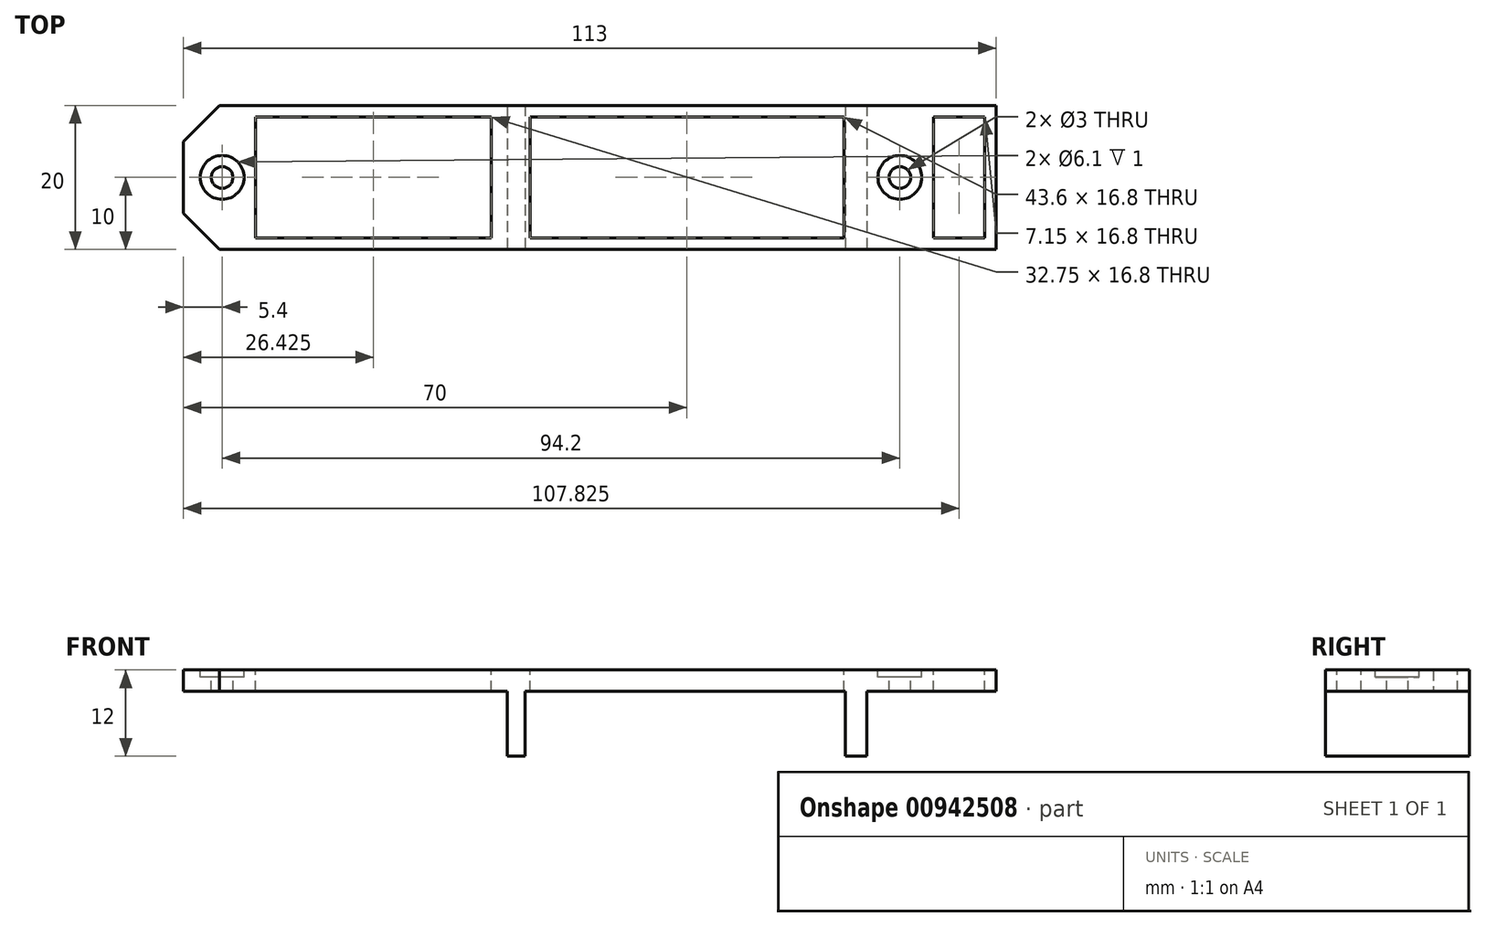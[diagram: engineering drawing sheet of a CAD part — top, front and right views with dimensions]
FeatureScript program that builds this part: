
annotation { "Feature Type Name" : "Feature", "Feature Type Description" : "" }
export const myFeature = defineFeature(function(context is Context, id is Id, definition is map)
    precondition{}
    {
        {
            var Q0;
            Q0=qCreatedBy(makeId("Top.planeOp"),FACE);
            var sketch = newSketch(context, id + "F0", { "sketchPlane" : qUnion([Q0])});
            skLineSegment(sketch, "E0.bottom", {"start": v(56.5, -10) * mm, "end": v(-56.5, -10) * mm});
            skLineSegment(sketch, "E0.top", {"start": v(56.5, 10) * mm, "end": v(-56.5, 10) * mm});
            skLineSegment(sketch, "E0.left", {"start": v(56.5, -10) * mm, "end": v(56.5, 10) * mm});
            skLineSegment(sketch, "E0.right", {"start": v(-56.5, -10) * mm, "end": v(-56.5, 10) * mm});
            skPoint(sketch, "E0.middle", {"position": v(0, 0) * mm});
            skSolve(sketch);
        }
        {
            var Q0;
            Q0=makeQuery(id+"F0.imprint","IMPRINT",FACE,{"disambiguationData":[TD([[makeQuery(id+"F0.imprint","IMPRINT",EDGE,{"derivedFrom":sQuery(id+"F0.wireOp",EDGE,"E0.bottom")}),-1.0]])]});
            extrude(context, id + "F1", {"entities" : qUnion([Q0]), "depth" : 3 * mm, "offsetDistance" : 25 * mm});
        }
        {
            var Q0;
            Q0=makeQuery(id+"F1.opExtrude","CAP_FACE",FACE,{"disambiguationData":[OSD([sQuery(id+"F0.wireOp",EDGE,"E0.bottom"),sQuery(id+"F0.wireOp",EDGE,"E0.top"),sQuery(id+"F0.wireOp",EDGE,"E0.left"),sQuery(id+"F0.wireOp",EDGE,"E0.right")])],"isStart":false});
            var sketch = newSketch(context, id + "F2", { "sketchPlane" : qUnion([Q0])});
            skLineSegment(sketch, "E1.bottom", {"start": v(35.5, 10) * mm, "end": v(38.5, 10) * mm});
            skLineSegment(sketch, "E1.top", {"start": v(35.5, -10) * mm, "end": v(38.5, -10) * mm});
            skLineSegment(sketch, "E1.left", {"start": v(35.5, 10) * mm, "end": v(35.5, -10) * mm});
            skLineSegment(sketch, "E1.right", {"start": v(38.5, 10) * mm, "end": v(38.5, -10) * mm});
            skPoint(sketch, "E1.middle", {"position": v(37, 0) * mm});
            skLineSegment(sketch, "E2.bottom", {"start": v(-9, 10) * mm, "end": v(-11.5, 10) * mm});
            skLineSegment(sketch, "E2.top", {"start": v(-9, -10) * mm, "end": v(-11.5, -10) * mm});
            skLineSegment(sketch, "E2.left", {"start": v(-9, 10) * mm, "end": v(-9, -10) * mm});
            skLineSegment(sketch, "E2.right", {"start": v(-11.5, 10) * mm, "end": v(-11.5, -10) * mm});
            skPoint(sketch, "E2.middle", {"position": v(-10.25, 0) * mm});
            skSolve(sketch);
        }
        {
            var Q0;
            Q0=makeQuery(id+"F2.imprint","IMPRINT",FACE,{"disambiguationData":[TD([[makeQuery(id+"F2.imprint","IMPRINT",EDGE,{"derivedFrom":sQuery(id+"F2.wireOp",EDGE,"E2.bottom")}),1.0]])]});
            var Q1;
            Q1=makeQuery(id+"F2.imprint","IMPRINT",FACE,{"disambiguationData":[TD([[makeQuery(id+"F2.imprint","IMPRINT",EDGE,{"derivedFrom":sQuery(id+"F2.wireOp",EDGE,"E1.bottom")}),1.0]])]});
            extrude(context, id + "F3", {"entities" : qUnion([Q0, Q1]), "operationType" : NewBodyOperationType.ADD, "oppositeDirection" : true, "depth" : 12 * mm, "offsetDistance" : 25 * mm});
        }
        {
            var Q0;
            {var subQ0=sQuery(id+"F0.wireOp",EDGE,"E0.top");var subQ1=sQuery(id+"F0.wireOp",EDGE,"E0.right");var subQ2=sQuery(id+"F0.wireOp",EDGE,"E0.bottom");Q0=makeQuery(id+"F3.boolean.opBoolean","SPLIT",FACE,{"disambiguationData":[TD([makeQuery(id+"F1.opExtrude","SWEPT_FACE",FACE,{"disambiguationData":[OSD([subQ1])]})])],"derivedFrom":makeQuery(id+"F1.opExtrude","CAP_FACE",FACE,{"disambiguationData":[OSD([subQ2,subQ0,sQuery(id+"F0.wireOp",EDGE,"E0.left"),subQ1])],"isStart":false})});}
            var sketch = newSketch(context, id + "F4", { "sketchPlane" : qUnion([Q0])});
            skCircle(sketch, "E3", {"center": v(-51.1, 0) * mm, "radius": 1.5 * mm});
            skCircle(sketch, "E4", {"center": v(43.1, 0) * mm, "radius": 1.5 * mm});
            skSolve(sketch);
        }
        {
            var Q0;
            Q0=makeQuery(id+"F4.imprint","IMPRINT",FACE,{"disambiguationData":[TD([[makeQuery(id+"F4.imprint","IMPRINT",EDGE,{"derivedFrom":sQuery(id+"F4.wireOp",EDGE,"E3")}),1.0]])]});
            var Q1;
            Q1=makeQuery(id+"F4.imprint","IMPRINT",FACE,{"disambiguationData":[TD([[makeQuery(id+"F4.imprint","IMPRINT",EDGE,{"derivedFrom":sQuery(id+"F4.wireOp",EDGE,"E4")}),1.0]])]});
            extrude(context, id + "F5", {"entities" : qUnion([Q0, Q1]), "operationType" : NewBodyOperationType.REMOVE, "endBound" : BoundingType.UP_TO_NEXT, "oppositeDirection" : true, "depth" : 25 * mm, "offsetDistance" : 25 * mm});
        }
        {
            var Q0;
            {var subQ0=sQuery(id+"F0.wireOp",EDGE,"E0.top");var subQ1=sQuery(id+"F0.wireOp",EDGE,"E0.right");var subQ2=sQuery(id+"F0.wireOp",EDGE,"E0.bottom");Q0=makeQuery(id+"F3.boolean.opBoolean","SPLIT",FACE,{"disambiguationData":[TD([makeQuery(id+"F1.opExtrude","SWEPT_FACE",FACE,{"disambiguationData":[OSD([subQ1])]})])],"derivedFrom":makeQuery(id+"F1.opExtrude","CAP_FACE",FACE,{"disambiguationData":[OSD([subQ2,subQ0,sQuery(id+"F0.wireOp",EDGE,"E0.left"),subQ1])],"isStart":false})});}
            var sketch = newSketch(context, id + "F6", { "sketchPlane" : qUnion([Q0])});
            skCircle(sketch, "E5", {"center": v(-51.1, 0) * mm, "radius": 3.05 * mm});
            skCircle(sketch, "E6", {"center": v(43.1, 0) * mm, "radius": 3.05 * mm});
            skSolve(sketch);
        }
        {
            var Q0;
            Q0=makeQuery(id+"F6.imprint","IMPRINT",FACE,{"disambiguationData":[TD([[makeQuery(id+"F6.imprint","IMPRINT",EDGE,{"derivedFrom":sQuery(id+"F6.wireOp",EDGE,"E5")}),1.0]])]});
            var Q1;
            Q1=makeQuery(id+"F6.imprint","IMPRINT",FACE,{"disambiguationData":[TD([[makeQuery(id+"F6.imprint","IMPRINT",EDGE,{"derivedFrom":sQuery(id+"F6.wireOp",EDGE,"E6")}),1.0]])]});
            extrude(context, id + "F7", {"entities" : qUnion([Q0, Q1]), "operationType" : NewBodyOperationType.REMOVE, "oppositeDirection" : true, "depth" : 1 * mm, "offsetDistance" : 25 * mm});
        }
        {
            var Q0;
            {var subQ0=sQuery(id+"F0.wireOp",EDGE,"E0.top");var subQ1=sQuery(id+"F0.wireOp",EDGE,"E0.bottom");Q0=makeQuery(id+"F3.boolean.opBoolean","SPLIT",FACE,{"disambiguationData":[TD([makeQuery(id+"F3.opExtrude","SWEPT_FACE",FACE,{"disambiguationData":[OSD([sQuery(id+"F2.wireOp",EDGE,"E1.left")])]})])],"derivedFrom":makeQuery(id+"F1.opExtrude","CAP_FACE",FACE,{"disambiguationData":[OSD([subQ1,subQ0,sQuery(id+"F0.wireOp",EDGE,"E0.left"),sQuery(id+"F0.wireOp",EDGE,"E0.right")])],"isStart":false})});}
            var sketch = newSketch(context, id + "F8", { "sketchPlane" : qUnion([Q0])});
            skLineSegment(sketch, "E7.bottom", {"start": v(35.3, -8.4) * mm, "end": v(-8.3, -8.4) * mm});
            skLineSegment(sketch, "E7.top", {"start": v(35.3, 8.4) * mm, "end": v(-8.3, 8.4) * mm});
            skLineSegment(sketch, "E7.left", {"start": v(35.3, -8.4) * mm, "end": v(35.3, 8.4) * mm});
            skLineSegment(sketch, "E7.right", {"start": v(-8.3, -8.4) * mm, "end": v(-8.3, 8.4) * mm});
            skPoint(sketch, "E7.middle", {"position": v(13.5, 0) * mm});
            skLineSegment(sketch, "E8.bottom", {"start": v(-13.7, -8.4) * mm, "end": v(-46.45, -8.4) * mm});
            skLineSegment(sketch, "E8.top", {"start": v(-13.7, 8.4) * mm, "end": v(-46.45, 8.4) * mm});
            skLineSegment(sketch, "E8.left", {"start": v(-13.7, -8.4) * mm, "end": v(-13.7, 8.4) * mm});
            skLineSegment(sketch, "E8.right", {"start": v(-46.45, -8.4) * mm, "end": v(-46.45, 8.4) * mm});
            skPoint(sketch, "E8.middle", {"position": v(-30.08, 0) * mm});
            skLineSegment(sketch, "E9.bottom", {"start": v(54.9, -8.4) * mm, "end": v(47.75, -8.4) * mm});
            skLineSegment(sketch, "E9.top", {"start": v(54.9, 8.4) * mm, "end": v(47.75, 8.4) * mm});
            skLineSegment(sketch, "E9.left", {"start": v(54.9, -8.4) * mm, "end": v(54.9, 8.4) * mm});
            skLineSegment(sketch, "E9.right", {"start": v(47.75, -8.4) * mm, "end": v(47.75, 8.4) * mm});
            skPoint(sketch, "E9.middle", {"position": v(51.32, 0) * mm});
            skSolve(sketch);
        }
        {
            var Q0;
            Q0=makeQuery(id+"F8.imprint","IMPRINT",FACE,{"disambiguationData":[TD([[makeQuery(id+"F8.imprint","IMPRINT",EDGE,{"derivedFrom":sQuery(id+"F8.wireOp",EDGE,"E8.bottom")}),-1.0]])]});
            var Q1;
            Q1=makeQuery(id+"F8.imprint","IMPRINT",FACE,{"disambiguationData":[TD([[makeQuery(id+"F8.imprint","IMPRINT",EDGE,{"derivedFrom":sQuery(id+"F8.wireOp",EDGE,"E7.bottom")}),-1.0]])]});
            var Q2;
            Q2=makeQuery(id+"F8.imprint","IMPRINT",FACE,{"disambiguationData":[TD([[makeQuery(id+"F8.imprint","IMPRINT",EDGE,{"derivedFrom":sQuery(id+"F8.wireOp",EDGE,"E9.bottom")}),-1.0]])]});
            extrude(context, id + "F9", {"entities" : qUnion([Q0, Q1, Q2]), "operationType" : NewBodyOperationType.REMOVE, "endBound" : BoundingType.UP_TO_NEXT, "oppositeDirection" : true, "depth" : 25 * mm, "offsetDistance" : 25 * mm});
        }
        {
            var Q0;
            Q0=makeQuery(id+"F1.opExtrude","SWEPT_EDGE",EDGE,{"disambiguationData":[OSD([sQuery(id+"F0.wireOp",EDGE,"E0.top"),sQuery(id+"F0.wireOp",EDGE,"E0.right")])]});
            var Q1;
            Q1=makeQuery(id+"F1.opExtrude","SWEPT_EDGE",EDGE,{"disambiguationData":[OSD([sQuery(id+"F0.wireOp",EDGE,"E0.bottom"),sQuery(id+"F0.wireOp",EDGE,"E0.right")])]});
            chamfer(context, id + "F10", {"entities" : qUnion([Q0, Q1]), "width" : 5 * mm, "tangentPropagation" : true});
        }
        {
            var Q0;
            Q0=makeQuery(id+"F1.opExtrude","SWEPT_BODY",BODY,{"disambiguationData":[OSD([sQuery(id+"F0.wireOp",EDGE,"E0.bottom"),sQuery(id+"F0.wireOp",EDGE,"E0.top"),sQuery(id+"F0.wireOp",EDGE,"E0.left"),sQuery(id+"F0.wireOp",EDGE,"E0.right")])]});
            var Q1;
            Q1=makeQuery(id+"F1.opExtrude","CAP_EDGE",EDGE,{"disambiguationData":[OSD([sQuery(id+"F0.wireOp",EDGE,"E0.bottom")])],"isStart":false});
            transform(context, id + "F11", {"entities" : qUnion([Q0]), "transformType" : TransformType.ROTATION, "transformAxis" : qUnion([Q1]), "angle" : 180 * degree, "makeCopy" : false});
        }
        {
            var Q0;
            Q0=makeQuery(id+"F1.opExtrude","SWEPT_BODY",BODY,{"disambiguationData":[OSD([sQuery(id+"F0.wireOp",EDGE,"E0.bottom"),sQuery(id+"F0.wireOp",EDGE,"E0.top"),sQuery(id+"F0.wireOp",EDGE,"E0.left"),sQuery(id+"F0.wireOp",EDGE,"E0.right")])]});
            var Q1;
            Q1=makeQuery(id+"F1.opExtrude","CAP_EDGE",EDGE,{"disambiguationData":[OSD([sQuery(id+"F0.wireOp",EDGE,"E0.bottom")])],"isStart":false});
            transform(context, id + "F12", {"entities" : qUnion([Q0]), "transformType" : TransformType.ROTATION, "transformAxis" : qUnion([Q1]), "angle" : 180 * degree, "makeCopy" : false});
        }
    });
